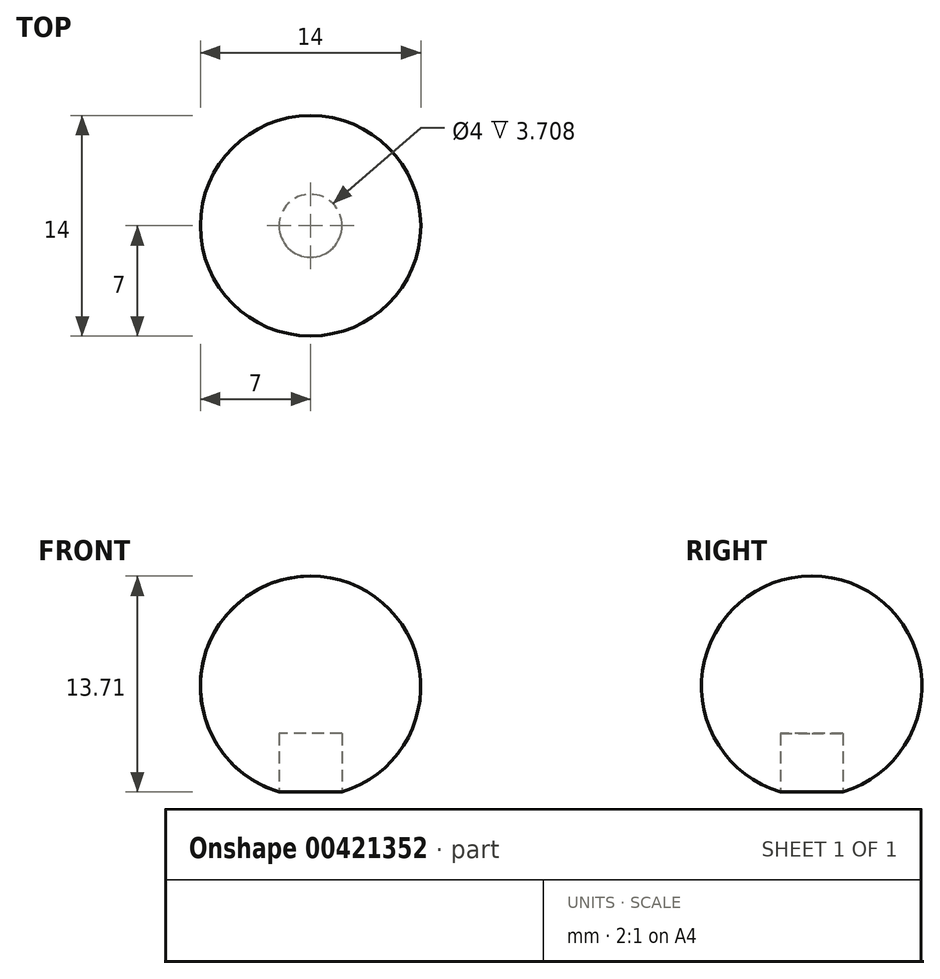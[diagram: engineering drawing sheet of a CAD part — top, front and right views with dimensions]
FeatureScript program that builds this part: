
annotation { "Feature Type Name" : "Feature", "Feature Type Description" : "" }
export const myFeature = defineFeature(function(context is Context, id is Id, definition is map)
    precondition{}
    {
        {
            var Q0;
            Q0=qCreatedBy(makeId("Front.planeOp"),FACE);
            var sketch = newSketch(context, id + "F0", { "sketchPlane" : qUnion([Q0])});
            skLineSegment(sketch, "E0", {"start": v(0, 7) * mm, "end": v(0, -7) * mm});
            skArc(sketch, "E1", {"start": v(0, 7) * mm, "mid": v(7, 0) * mm, "end": v(0, -7) * mm});
            skSolve(sketch);
        }
        {
            var Q0;
            Q0 = qSketchRegion(id + "F0", true);
            var Q1;
            Q1=sQuery(id+"F0.wireOp",EDGE,"E0");
            revolve(context, id + "F1", {"entities" : qUnion([Q0]), "axis" : qUnion([Q1]), "revolveType" : RevolveType.FULL});
        }
        {
            var Q0;
            Q0=qCreatedBy(makeId("Top.planeOp"),FACE);
            cPlane(context, id + "F2", {"entities" : qUnion([Q0]), "cplaneType" : CPlaneType.OFFSET, "offset" : 7 * mm, "oppositeDirection" : true, "width" : 152.4 * mm, "height" : 152.4 * mm});
        }
        {
            var Q0;
            Q0=qCreatedBy(id+"F2.planeOp",FACE);
            var sketch = newSketch(context, id + "F3", { "sketchPlane" : qUnion([Q0])});
            skCircle(sketch, "E2", {"center": v(0, 0) * mm, "radius": 2 * mm});
            skSolve(sketch);
        }
        {
            var Q0;
            Q0 = qSketchRegion(id + "F3", true);
            extrude(context, id + "F4", {"entities" : qUnion([Q0]), "operationType" : NewBodyOperationType.REMOVE, "depth" : 4 * mm});
        }
    });
